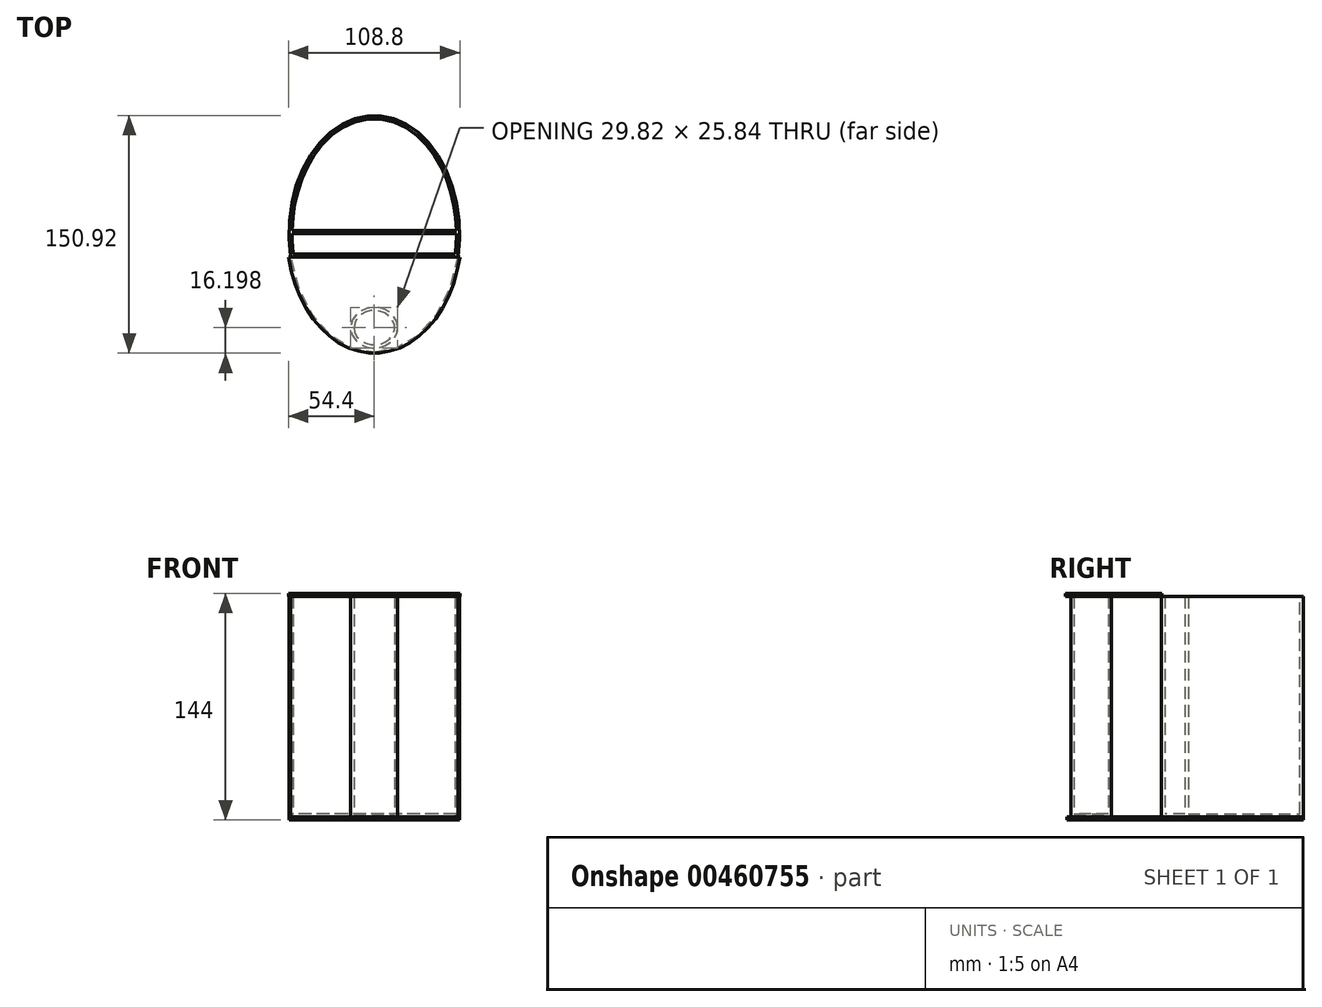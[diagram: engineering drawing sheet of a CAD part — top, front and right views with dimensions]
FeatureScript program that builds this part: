
annotation { "Feature Type Name" : "Feature", "Feature Type Description" : "" }
export const myFeature = defineFeature(function(context is Context, id is Id, definition is map)
    precondition{}
    {
        {
            var Q0;
            Q0=qCreatedBy(makeId("Top.planeOp"),FACE);
            var sketch = newSketch(context, id + "F0", { "sketchPlane" : qUnion([Q0])});
            skEllipse(sketch, "E0", {"center": v(0, 0) * mm, "majorRadius": 75.06 * mm, "minorRadius": 54.22 * mm, "majorAxis": v(0, -1)});
            skLineSegment(sketch, "E1", {"start": v(54.22, 0) * mm, "end": v(-54.22, 0) * mm});
            skEllipse(sketch, "E2", {"center": v(0, -59.66) * mm, "majorRadius": 14.91 * mm, "minorRadius": 12.92 * mm, "majorAxis": v(1, 0)});
            skLineSegment(sketch, "E3", {"start": v(53.14, -14.92) * mm, "end": v(-53.14, -14.92) * mm});
            skPoint(sketch, "E4.end.orphan", {"position": v(0, -14.92) * mm});
            skSolve(sketch);
        }
        {
            var Q0;
            {var subQ0=sQuery(id+"F0.wireOp",EDGE,"E1");var subQ1=sQuery(id+"F0.wireOp",EDGE,"E0");var subQ2=makeQuery(id+"F0.imprint","INTERSECT",VERTEX,{"disambiguationData":[OD(0.0)],"derivedFrom":[subQ1,subQ0]});Q0=makeQuery(id+"F0.imprint","IMPRINT",FACE,{"disambiguationData":[TD([[makeQuery(id+"F0.imprint","IMPRINT",EDGE,{"disambiguationData":[TD([[subQ2,-1.0]])],"derivedFrom":subQ1}),1.0]])]});}
            extrude(context, id + "F1", {"entities" : qUnion([Q0]), "depth" : 140 * mm, "offsetDistance" : 25 * mm});
        }
        {
            var Q0;
            Q0=makeQuery(id+"F1.opExtrude","CAP_FACE",FACE,{"disambiguationData":[OSD([sQuery(id+"F0.wireOp",EDGE,"E0"),sQuery(id+"F0.wireOp",EDGE,"E1")])],"isStart":false});
            shell(context, id + "F2", {"entities" : qUnion([Q0]), "thickness" : 2 * mm});
        }
        {
            var Q0;
            {var subQ0=sQuery(id+"F0.wireOp",EDGE,"E1");Q0=makeQuery(id+"F0.imprint","IMPRINT",FACE,{"disambiguationData":[TD([[makeQuery(id+"F0.imprint","IMPRINT",EDGE,{"derivedFrom":subQ0}),1.0]])]});}
            extrude(context, id + "F3", {"entities" : qUnion([Q0]), "operationType" : NewBodyOperationType.ADD, "depth" : 140 * mm, "offsetDistance" : 25 * mm});
        }
        {
            var Q0;
            {var subQ0=sQuery(id+"F0.wireOp",EDGE,"E1");var subQ1=sQuery(id+"F0.wireOp",EDGE,"E0");Q0=makeQuery(id+"F3.boolean.opBoolean","MERGE",FACE,{"derivedFrom":[makeQuery(id+"F1.opExtrude","CAP_FACE",FACE,{"disambiguationData":[OSD([subQ1,subQ0])],"isStart":false}),makeQuery(id+"F3.opExtrude","CAP_FACE",FACE,{"disambiguationData":[OSD([subQ1,subQ0,sQuery(id+"F0.wireOp",EDGE,"E3")])],"isStart":false})]});}
            shell(context, id + "F4", {"entities" : qUnion([Q0]), "thickness" : 2 * mm});
        }
        {
            var Q0;
            Q0=makeQuery(id+"F0.imprint","IMPRINT",FACE,{"disambiguationData":[TD([[makeQuery(id+"F0.imprint","IMPRINT",EDGE,{"derivedFrom":sQuery(id+"F0.wireOp",EDGE,"E2")}),1.0]])]});
            var Q1;
            Q1=sQuery(id+"F0.wireOp",EDGE,"E2");
            extrude(context, id + "F5", {"entities" : qUnion([Q0]), "surfaceEntities" : qUnion([Q1]), "depth" : 140 * mm, "offsetDistance" : 25 * mm});
        }
        {
            var Q0;
            Q0=makeQuery(id+"F5.opExtrude","CAP_FACE",FACE,{"disambiguationData":[OSD([sQuery(id+"F0.wireOp",EDGE,"E2")])],"isStart":false});
            shell(context, id + "F6", {"entities" : qUnion([Q0]), "thickness" : 2 * mm});
        }
        {
            var Q0;
            Q0 = qSketchRegion(id + "F0", true);
            extrude(context, id + "F7", {"entities" : qUnion([Q0]), "oppositeDirection" : true, "depth" : 2 * mm, "offsetDistance" : 25 * mm});
        }
        {
            var Q0;
            Q0=makeQuery(id+"F5.opExtrude","CAP_FACE",FACE,{"disambiguationData":[OSD([sQuery(id+"F0.wireOp",EDGE,"E2")])],"isStart":true});
            extrude(context, id + "F8", {"entities" : qUnion([Q0]), "depth" : 2 * mm, "offsetDistance" : 25 * mm});
        }
        {
            var Q0;
            Q0=qCreatedBy(makeId("Top.planeOp"),FACE);
            cPlane(context, id + "F9", {"entities" : qUnion([Q0]), "cplaneType" : CPlaneType.OFFSET, "offset" : 140 * mm, "width" : 150 * mm, "height" : 150 * mm});
        }
        {
            var Q0;
            Q0=qCreatedBy(id+"F9.planeOp",FACE);
            var sketch = newSketch(context, id + "F10", { "sketchPlane" : qUnion([Q0])});
            skEllipticalArc(sketch, "E5", {});
            skLineSegment(sketch, "E6", {"start": v(-55.46, 0) * mm, "end": v(55.46, 0) * mm});
            skLineSegment(sketch, "E7", {"start": v(0, -14.72) * mm, "end": v(54.4, -14.72) * mm});
            skLineSegment(sketch, "E8", {"start": v(0, -14.72) * mm, "end": v(-54.4, -14.72) * mm});
            skEllipticalArc(sketch, "E9.trimOffspring", {});
            skLineSegment(sketch, "E10.bottom", {"start": v(27.4, -10.42) * mm, "end": v(-27.4, -10.42) * mm});
            skLineSegment(sketch, "E10.top", {"start": v(27.4, -3.07) * mm, "end": v(-27.4, -3.07) * mm});
            skLineSegment(sketch, "E10.left", {"start": v(27.4, -10.42) * mm, "end": v(27.4, -3.07) * mm});
            skLineSegment(sketch, "E10.right", {"start": v(-27.4, -10.42) * mm, "end": v(-27.4, -3.07) * mm});
            skPoint(sketch, "E10.middle", {"position": v(0, -6.75) * mm});
            const initialGuessF10  = {"E5": [0, 0, 0, -1, 0.0758572518825531, 0.05545511899439339, 1.5707963267948966, 4.71238898038469], "E9.trimOffspring": [0, 0, 0, -1, 0.0758572518825531, 0.05545511899439339, 4.907633642052568, 1.3755516651270179]};
            skSetInitialGuess(sketch, initialGuessF10);
            skSolve(sketch);
        }
        {
            var Q0;
            Q0=makeQuery(id+"F10.imprint","IMPRINT",FACE,{"disambiguationData":[TD([[makeQuery(id+"F10.imprint","IMPRINT",EDGE,{"derivedFrom":sQuery(id+"F10.wireOp",EDGE,"E7")}),-1.0]])]});
            extrude(context, id + "F11", {"entities" : qUnion([Q0]), "depth" : 2 * mm, "offsetDistance" : 25 * mm});
        }
        {
            var Q0;
            Q0=qCreatedBy(id+"F9.planeOp",FACE);
            cPlane(context, id + "F12", {"entities" : qUnion([Q0]), "cplaneType" : CPlaneType.OFFSET, "offset" : 25 * mm, "width" : 150 * mm, "height" : 150 * mm});
        }
        {
            var Q0;
            Q0=qCreatedBy(id+"F12.planeOp",FACE);
            var sketch = newSketch(context, id + "F13", { "sketchPlane" : qUnion([Q0])});
            skCircle(sketch, "E11", {"center": v(0, 54.22) * mm, "radius": 7.15 * mm});
            skSolve(sketch);
        }
        {
            var Q0;
            Q0=makeQuery(id+"F10.imprint","IMPRINT",FACE,{"disambiguationData":[TD([[makeQuery(id+"F10.imprint","IMPRINT",EDGE,{"derivedFrom":sQuery(id+"F10.wireOp",EDGE,"E5")}),1.0]])]});
            var Q1;
            Q1 = qSketchRegion(id + "F13", true);
            var Q2;
            Q2=makeQuery(id+"F10.imprint","IMPRINT",FACE,{"disambiguationData":[TD([[makeQuery(id+"F10.imprint","IMPRINT",EDGE,{"derivedFrom":sQuery(id+"F10.wireOp",EDGE,"E5")}),1.0]])]});
            var Q3;
            Q3=sQuery(id+"F13.wireOp",EDGE,"E11");
            loft(context, id + "F14", {"bodyType" : ToolBodyType.SURFACE, "sheetProfilesArray" : [{ "sheetProfileEntities" : qUnion([Q0]) }, { "sheetProfileEntities" : qUnion([Q1]) }], "wireProfilesArray" : [{ "wireProfileEntities" : qUnion([Q2]) }, { "wireProfileEntities" : qUnion([Q3]) }]});
        }
    });
